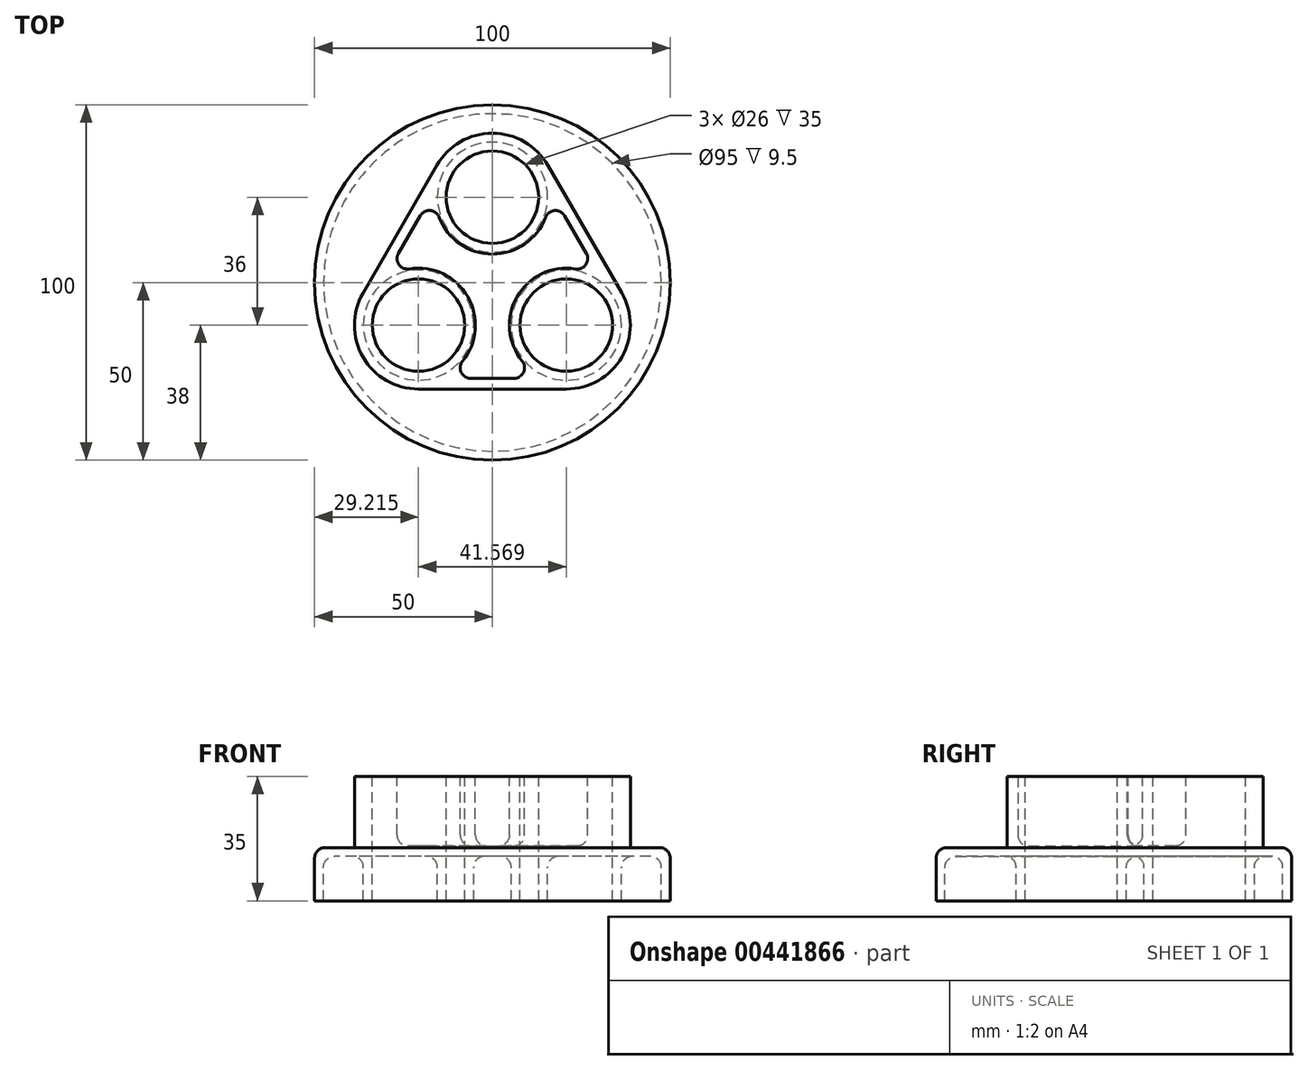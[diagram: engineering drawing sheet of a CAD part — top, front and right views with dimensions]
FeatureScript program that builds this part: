
annotation { "Feature Type Name" : "Feature", "Feature Type Description" : "" }
export const myFeature = defineFeature(function(context is Context, id is Id, definition is map)
    precondition{}
    {
        {
            var Q0;
            Q0=qCreatedBy(makeId("Top.planeOp"),FACE);
            var sketch = newSketch(context, id + "F0", { "sketchPlane" : qUnion([Q0])});
            skCircle(sketch, "E0", {"center": v(0, 0) * mm, "radius": 50 * mm});
            skCircle(sketch, "E1", {"center": v(0, 0) * mm, "radius": 24 * mm, "construction": true});
            skCircle(sketch, "E2.1.0", {"center": v(-20.78, -12) * mm, "radius": 18 * mm});
            skCircle(sketch, "E2.1.1", {"center": v(-20.78, -12) * mm, "radius": 13 * mm});
            skLineSegment(sketch, "E3", {"start": v(-20.78, -30) * mm, "end": v(20.78, -30) * mm});
            skLineSegment(sketch, "E4.1.0", {"start": v(36.37, -3) * mm, "end": v(15.59, 33) * mm});
            skCircle(sketch, "E4.1.1", {"center": v(20.78, -12) * mm, "radius": 13 * mm});
            skCircle(sketch, "E4.1.2", {"center": v(20.78, -12) * mm, "radius": 18 * mm});
            skLineSegment(sketch, "E4.2.0", {"start": v(-15.59, 33) * mm, "end": v(-36.37, -3) * mm});
            skCircle(sketch, "E4.2.1", {"center": v(0, 24) * mm, "radius": 13 * mm});
            skCircle(sketch, "E4.2.2", {"center": v(0, 24) * mm, "radius": 18 * mm});
            skSolve(sketch);
        }
        {
            var Q0;
            Q0 = qSketchRegion(id + "F0", true);
            var Q1;
            Q1=makeQuery(id+"F0.imprint","IMPRINT",FACE,{"disambiguationData":[TD([[makeQuery(id+"F0.imprint","IMPRINT",EDGE,{"derivedFrom":sQuery(id+"F0.wireOp",EDGE,"E2.1.1")}),-1.0]])]});
            var Q2;
            Q2=makeQuery(id+"F0.imprint","IMPRINT",FACE,{"disambiguationData":[TD([[makeQuery(id+"F0.imprint","IMPRINT",EDGE,{"derivedFrom":sQuery(id+"F0.wireOp",EDGE,"E4.2.1")}),-1.0]])]});
            var Q3;
            {var subQ1=sQuery(id+"F0.wireOp",EDGE,"E3");Q3=makeQuery(id+"F0.imprint","IMPRINT",FACE,{"disambiguationData":[TD([[makeQuery(id+"F0.imprint","IMPRINT",EDGE,{"derivedFrom":subQ1}),1.0]])]});}
            var Q4;
            Q4=makeQuery(id+"F0.imprint","IMPRINT",FACE,{"disambiguationData":[TD([[makeQuery(id+"F0.imprint","IMPRINT",EDGE,{"derivedFrom":sQuery(id+"F0.wireOp",EDGE,"E4.1.1")}),-1.0]])]});
            var Q5;
            Q5=makeQuery(id+"F0.imprint","IMPRINT",FACE,{"disambiguationData":[TD([[makeQuery(id+"F0.imprint","IMPRINT",EDGE,{"derivedFrom":sQuery(id+"F0.wireOp",EDGE,"E0")}),1.0]])]});
            extrude(context, id + "F1", {"entities" : qUnion([Q0, Q1, Q2, Q3, Q4, Q5]), "oppositeDirection" : true, "depth" : 15 * mm});
        }
        {
            var Q0;
            Q0=makeQuery(id+"F1.opExtrude","CAP_FACE",FACE,{"disambiguationData":[OSD([sQuery(id+"F0.wireOp",EDGE,"E0"),sQuery(id+"F0.wireOp",EDGE,"E2.1.1"),sQuery(id+"F0.wireOp",EDGE,"E4.1.1"),sQuery(id+"F0.wireOp",EDGE,"E4.2.1")])],"isStart":false});
            shell(context, id + "F2", {"entities" : qUnion([Q0]), "thickness" : 2.5 * mm});
        }
        {
            var Q0;
            Q0=makeQuery(id+"F0.imprint","IMPRINT",FACE,{"disambiguationData":[TD([[makeQuery(id+"F0.imprint","IMPRINT",EDGE,{"derivedFrom":sQuery(id+"F0.wireOp",EDGE,"E4.2.1")}),-1.0]])]});
            var Q1;
            Q1=makeQuery(id+"F0.imprint","IMPRINT",FACE,{"disambiguationData":[TD([[makeQuery(id+"F0.imprint","IMPRINT",EDGE,{"derivedFrom":sQuery(id+"F0.wireOp",EDGE,"E2.1.1")}),-1.0]])]});
            var Q2;
            Q2=makeQuery(id+"F0.imprint","IMPRINT",FACE,{"disambiguationData":[TD([[makeQuery(id+"F0.imprint","IMPRINT",EDGE,{"derivedFrom":sQuery(id+"F0.wireOp",EDGE,"E4.1.1")}),-1.0]])]});
            var Q3;
            {var subQ1=sQuery(id+"F0.wireOp",EDGE,"E3");Q3=makeQuery(id+"F0.imprint","IMPRINT",FACE,{"disambiguationData":[TD([[makeQuery(id+"F0.imprint","IMPRINT",EDGE,{"derivedFrom":subQ1}),1.0]])]});}
            extrude(context, id + "F3", {"entities" : qUnion([Q0, Q1, Q2, Q3]), "operationType" : NewBodyOperationType.ADD, "depth" : 20 * mm});
        }
        {
            var Q0;
            Q0=makeQuery(id+"F3.opExtrude","CAP_FACE",FACE,{"disambiguationData":[OSD([sQuery(id+"F0.wireOp",EDGE,"E2.1.0"),sQuery(id+"F0.wireOp",EDGE,"E2.1.1"),sQuery(id+"F0.wireOp",EDGE,"E3"),sQuery(id+"F0.wireOp",EDGE,"E4.1.0"),sQuery(id+"F0.wireOp",EDGE,"E4.1.1"),sQuery(id+"F0.wireOp",EDGE,"E4.1.2"),sQuery(id+"F0.wireOp",EDGE,"E4.2.0"),sQuery(id+"F0.wireOp",EDGE,"E4.2.1"),sQuery(id+"F0.wireOp",EDGE,"E4.2.2")])],"isStart":false});
            shell(context, id + "F4", {"entities" : qUnion([Q0]), "thickness" : 3 * mm});
        }
        {
            var Q0;
            {var subQ0=sQuery(id+"F0.wireOp",EDGE,"E2.1.1");Q0=makeQuery(id+"F4.opShell","TWEAK_EDGE",EDGE,{"derivedFrom":[makeQuery(id+"F3.opExtrude","SWEPT_FACE",FACE,{"disambiguationData":[OSD([sQuery(id+"F0.wireOp",EDGE,"E3")])]}),makeQuery(id+"F3.boolean.opBoolean","MERGE",FACE,{"derivedFrom":[makeQuery(id+"F1.opExtrude","SWEPT_FACE",FACE,{"disambiguationData":[OSD([subQ0])]}),makeQuery(id+"F3.opExtrude","SWEPT_FACE",FACE,{"disambiguationData":[OSD([subQ0])]})]})]});}
            var Q1;
            {var subQ0=sQuery(id+"F0.wireOp",EDGE,"E2.1.1");Q1=makeQuery(id+"F4.opShell","TWEAK_EDGE",EDGE,{"derivedFrom":[makeQuery(id+"F3.opExtrude","SWEPT_FACE",FACE,{"disambiguationData":[OSD([sQuery(id+"F0.wireOp",EDGE,"E4.2.0")])]}),makeQuery(id+"F3.boolean.opBoolean","MERGE",FACE,{"derivedFrom":[makeQuery(id+"F1.opExtrude","SWEPT_FACE",FACE,{"disambiguationData":[OSD([subQ0])]}),makeQuery(id+"F3.opExtrude","SWEPT_FACE",FACE,{"disambiguationData":[OSD([subQ0])]})]})]});}
            var Q2;
            {var subQ0=sQuery(id+"F0.wireOp",EDGE,"E4.1.1");Q2=makeQuery(id+"F4.opShell","TWEAK_EDGE",EDGE,{"derivedFrom":[makeQuery(id+"F3.opExtrude","SWEPT_FACE",FACE,{"disambiguationData":[OSD([sQuery(id+"F0.wireOp",EDGE,"E4.1.0")])]}),makeQuery(id+"F3.boolean.opBoolean","MERGE",FACE,{"derivedFrom":[makeQuery(id+"F1.opExtrude","SWEPT_FACE",FACE,{"disambiguationData":[OSD([subQ0])]}),makeQuery(id+"F3.opExtrude","SWEPT_FACE",FACE,{"disambiguationData":[OSD([subQ0])]})]})]});}
            var Q3;
            {var subQ0=sQuery(id+"F0.wireOp",EDGE,"E4.2.1");Q3=makeQuery(id+"F4.opShell","TWEAK_EDGE",EDGE,{"derivedFrom":[makeQuery(id+"F3.opExtrude","SWEPT_FACE",FACE,{"disambiguationData":[OSD([sQuery(id+"F0.wireOp",EDGE,"E4.1.0")])]}),makeQuery(id+"F3.boolean.opBoolean","MERGE",FACE,{"derivedFrom":[makeQuery(id+"F1.opExtrude","SWEPT_FACE",FACE,{"disambiguationData":[OSD([subQ0])]}),makeQuery(id+"F3.opExtrude","SWEPT_FACE",FACE,{"disambiguationData":[OSD([subQ0])]})]})]});}
            var Q4;
            {var subQ0=sQuery(id+"F0.wireOp",EDGE,"E4.1.1");Q4=makeQuery(id+"F4.opShell","TWEAK_EDGE",EDGE,{"derivedFrom":[makeQuery(id+"F3.opExtrude","SWEPT_FACE",FACE,{"disambiguationData":[OSD([sQuery(id+"F0.wireOp",EDGE,"E3")])]}),makeQuery(id+"F3.boolean.opBoolean","MERGE",FACE,{"derivedFrom":[makeQuery(id+"F1.opExtrude","SWEPT_FACE",FACE,{"disambiguationData":[OSD([subQ0])]}),makeQuery(id+"F3.opExtrude","SWEPT_FACE",FACE,{"disambiguationData":[OSD([subQ0])]})]})]});}
            var Q5;
            {var subQ0=sQuery(id+"F0.wireOp",EDGE,"E4.2.1");Q5=makeQuery(id+"F4.opShell","TWEAK_EDGE",EDGE,{"derivedFrom":[makeQuery(id+"F3.opExtrude","SWEPT_FACE",FACE,{"disambiguationData":[OSD([sQuery(id+"F0.wireOp",EDGE,"E4.2.0")])]}),makeQuery(id+"F3.boolean.opBoolean","MERGE",FACE,{"derivedFrom":[makeQuery(id+"F1.opExtrude","SWEPT_FACE",FACE,{"disambiguationData":[OSD([subQ0])]}),makeQuery(id+"F3.opExtrude","SWEPT_FACE",FACE,{"disambiguationData":[OSD([subQ0])]})]})]});}
            var Q6;
            {var subQ0=sQuery(id+"F0.wireOp",EDGE,"E4.2.1");var subQ1=sQuery(id+"F0.wireOp",EDGE,"E4.1.1");var subQ2=sQuery(id+"F0.wireOp",EDGE,"E2.1.1");var subQ3=sQuery(id+"F0.wireOp",EDGE,"E0");Q6=makeQuery(id+"F2.opShell","OFFSET_FACE",FACE,{"disambiguationData":[OSD([subQ3,subQ2,subQ1,subQ0]),TDD([makeQuery(id+"F1.opExtrude","CAP_FACE",FACE,{"disambiguationData":[OSD([subQ3,subQ2,subQ1,subQ0])],"isStart":true})])]});}
            var Q7;
            Q7=makeQuery(id+"F4.opShell","OFFSET_FACE",FACE,{"disambiguationData":[OSD([sQuery(id+"F0.wireOp",EDGE,"E0"),sQuery(id+"F0.wireOp",EDGE,"E2.1.1"),sQuery(id+"F0.wireOp",EDGE,"E4.1.1"),sQuery(id+"F0.wireOp",EDGE,"E4.2.1")])]});
            var Q8;
            Q8=makeQuery(id+"F3.opExtrude","CAP_EDGE",EDGE,{"disambiguationData":[OSD([sQuery(id+"F0.wireOp",EDGE,"E3")])],"isStart":true});
            fillet(context, id + "F5", {"entities" : qUnion([Q0, Q1, Q2, Q3, Q4, Q5, Q6, Q7, Q8]), "radius" : 3 * mm, "tangentPropagation" : true, "allowEdgeOverflow" : false});
        }
        {
            var Q0;
            Q0=makeQuery(id+"F1.opExtrude","CAP_EDGE",EDGE,{"disambiguationData":[OSD([sQuery(id+"F0.wireOp",EDGE,"E0")])],"isStart":true});
            fillet(context, id + "F6", {"entities" : qUnion([Q0]), "radius" : 3 * mm, "tangentPropagation" : true, "allowEdgeOverflow" : false});
        }
    });
